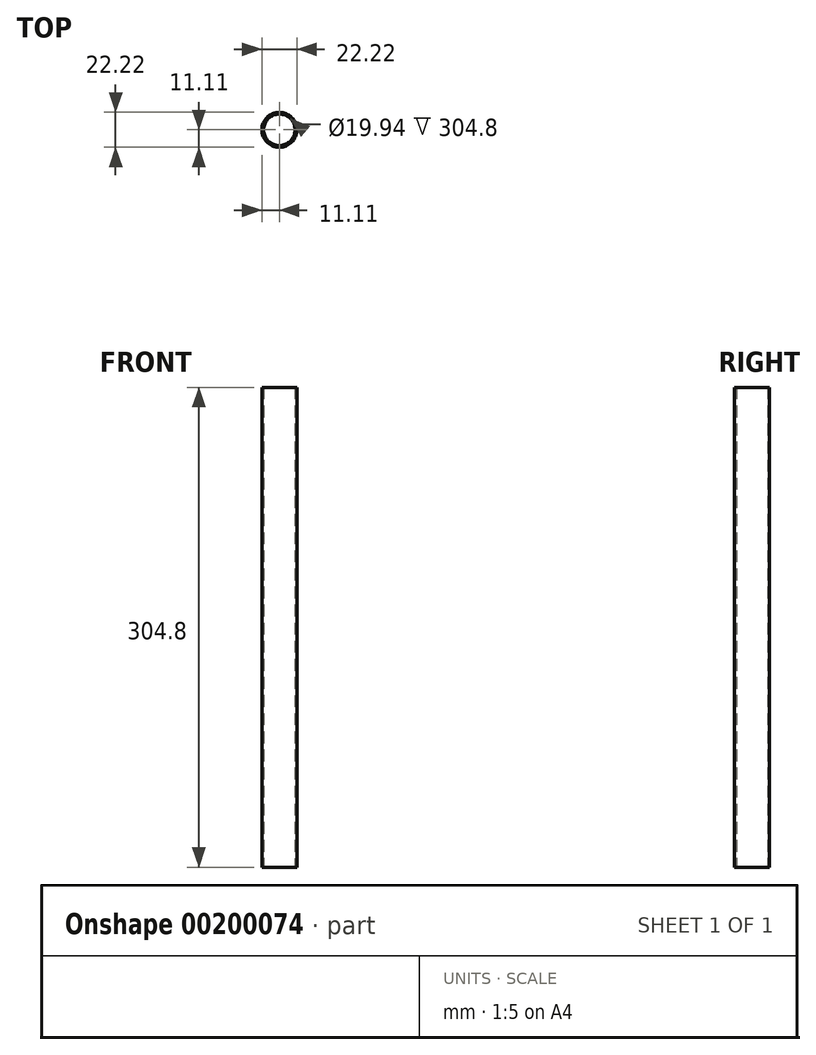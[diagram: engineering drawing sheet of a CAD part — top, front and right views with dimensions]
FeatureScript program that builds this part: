
annotation { "Feature Type Name" : "Feature", "Feature Type Description" : "" }
export const myFeature = defineFeature(function(context is Context, id is Id, definition is map)
    precondition{}
    {
        {
            var Q0;
            Q0=qCreatedBy(makeId("Top.planeOp"),FACE);
            var sketch = newSketch(context, id + "F0", { "sketchPlane" : qUnion([Q0])});
            skCircle(sketch, "E0", {"center": v(0, 0) * mm, "radius": 9.97 * mm});
            skCircle(sketch, "E1.0", {"center": v(0, 0) * mm, "radius": 11.11 * mm});
            skSolve(sketch);
        }
        {
            var Q0;
            Q0=makeQuery(id+"F0.imprint","IMPRINT",FACE,{"disambiguationData":[TD([[makeQuery(id+"F0.imprint","IMPRINT",EDGE,{"derivedFrom":sQuery(id+"F0.wireOp",EDGE,"E0")}),-1.0]])]});
            extrude(context, id + "F1", {"entities" : qUnion([Q0]), "depth" : 304.8 * mm});
        }
    });
